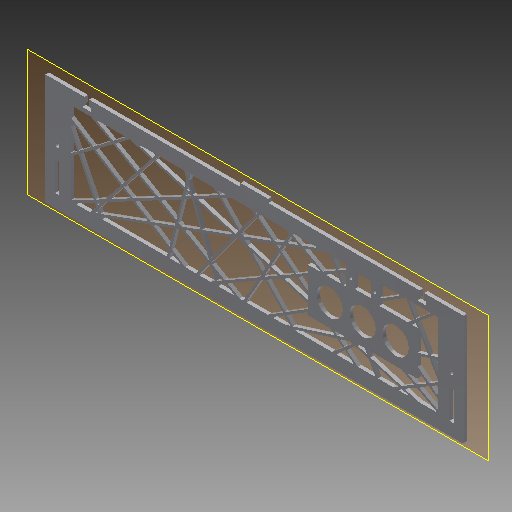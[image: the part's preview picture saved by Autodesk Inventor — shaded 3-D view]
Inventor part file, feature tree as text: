
AUTODESK INVENTOR PART (.ipt)
format: ipt  version: 2019 (Build 230136000, 136)  size: 1,500,160 bytes
history: native  units: in
note: dims shown in document units (in); Inventor stores cm internally (conversion verified against a paired STEP export)
features: fillet x12, extrude x11, sketch x10, other x9, reference x9, hole x3, plane x1
ambient origin geometry x8: Origin, YZ Plane, XZ Plane, XY Plane, X Axis, Y Axis, Z Axis, Center Point
bodies: Solid1 (feature_tree)
feature tree (55):
  plane  "Work Plane1"
  extrude  "BackPanel"  Depth=0.0394in
  fillet  "CornerFillet"  Radius=0.475in
  extrude  "ScrewSlotExtrusion"  Depth=0.3265in
  fillet  "SlotFillets"  Radius=0.1234in
  hole  "Hole1"  [1 undecoded]
  extrude  "BottomTab"  Depth=0.1234in
  fillet  "BottomTabFillet"  Radius=0.125in
  extrude  "Slots"  Depth=1.0in
  fillet  "Fillet4"  Radius=0.0197in
  extrude  "InsideGap"  Depth=1.0in
  fillet  "InsideGapFillet"  Radius=0.125in
  extrude  "Hash1"  Depth=1.054in
  extrude  "Hash2"  Depth=1.054in
  extrude  "BackButtonMount"  Depth=0.125in TaperAngle=0.0deg
  hole  "BackButtonHoles"  [1 undecoded]
  extrude  "USBPortMount"  Depth=0.5in
  extrude  "USBPortHole"  Depth=0.5in
  hole  "USBPortScrewHoles"  [1 undecoded]
  fillet  "GridFillets1"  Radius=0.5in
  fillet  "GridFillets2"  Radius=1.0in
  fillet  "GridFillets3"  Radius=0.0197in
  fillet  "GridFillets4"  Radius=0.0882in
  fillet  "GridFillets5"  Radius=1.15in
  fillet  "GridFillets6"  Radius=2.8in
  fillet  "GridFillets7"  Radius=4.0072in
  extrude  "SmallHoleRemoval"  Depth=0.125in
  sketch  "Sketch1"  dims[d0=0.125in d1=0.0in d2=0.0394in d3=0.475in]
  other  "ScrewSlotSketch"
  reference  "Reference1"
  reference  "Reference2"
  reference  "Reference3"
  other  "ScrewHoleSketch"
  reference  "Reference4"
  reference  "Reference5"
  reference  "Reference6"
  reference  "Reference7"
  other  "BottomTabSketch"
  other  "SlotSketch"
  sketch  "Sketch6"  dims[d5=0.1495in d7=0.3265in d8=0.1234in]
  reference  "Reference18"
  reference  "Reference19"
  sketch  "Sketch7"  dims[d9=0.475in d10=0.1495in]
  sketch  "Sketch8"  dims[d12=0.3265in d13=0.1234in d20=0.125in d21=0.0in]
  sketch  "Sketch9"  dims[d22=1.0in d23=1.0in d24=0.0197in]
  sketch  "Sketch10"  dims[d25=0.1495in]
  sketch  "Sketch12"  dims[d26=0.75in d27=0.375in d28=0.25in d29=0.5635in d30=1.0in d31=0.8108in d32=1.0in d34=0.125in d35=0.0in]
  sketch  "Sketch13"  dims[d36=0.0197in d37=1.054in]
  sketch  "Sketch14"  dims[d39=0.149in d40=1.054in]
  sketch  "Sketch15"  dims[d41=0.149in d42=0.125in d43=0.0in d44=0.0197in d45=0.5in d46=0.5in d47=0.5in d48=0.5in d49=1.0in d50=0.0in d51=0.0197in d52=0.0882in d53=1.15in d54=2.8in d55=4.0072in d56=5.1478in d57=7.3764in d58=8.8266in d59=11.0in d60=2.102in d61=0.4077in d62=0.962in d63=1.017in d64=150.0deg d65=1.0994in d66=0.8225in d67=1.0444in d68=0.7174in d69=0.9826in d70=0.08in d71=0.08in d72=0.08in d73=0.08in d74=0.08in d75=0.08in d76=0.08in d77=0.08in d78=0.08in d79=0.08in d80=6.3348in d81=0.8684in d82=9.9487in d83=0.8831in d84=0.08in d85=0.125in d86=0.0in d87=0.8208in d88=0.4592in d89=1.0588in d90=0.8406in d91=0.702in d92=2.054in d93=150.0deg d94=1.124in d95=4.025in d96=0.7627in d97=5.1in d98=0.916in d99=6.426in d100=0.9702in d101=7.6562in d103=9.2721in d104=0.8139in d105=9.8in d106=0.9786in d107=11.9921in d108=120.0deg d109=0.08in d111=0.08in d112=0.08in d114=0.08in d115=0.08in d116=0.08in d117=0.08in d118=0.08in d119=0.08in d120=0.125in d121=0.0in d122=1.312in d123=0.4978in d124=0.08in d125=0.08in d126=0.08in d127=1.1811in d129=1.1811in d130=2.0in d131=0.7874in d132=0.7874in d133=0.125in d134=0.0in d135=1.1811in d137=1.1811in d138=0.9449in d139=0.75in d140=0.375in d141=0.25in d142=0.5635in d143=1.0in d144=0.8108in d152=1.1811in d156=0.125in d157=0.0in d158=0.5712in d160=0.5318in d161=0.125in d162=0.0in d163=0.8661in d165=0.129in d166=0.75in d167=0.225in d168=0.25in d169=0.5635in d170=1.0in d171=0.8108in d172=0.0197in d173=0.0197in d174=0.0197in d175=0.0197in d176=0.0197in d177=0.0197in d178=0.0197in d179=0.125in d180=0.0in]
  parser-record x1  (decoder bookkeeping rows leaked as tree rows — omitted from the tree; the rows remain in map.json)
  other  "ArcadeController.iam"
  other  "Panel_side:2"
  other  "Panel_side:1"
  other  "BottomPanel:1"
note: 3 required parameter values undecoded (feature->parameter linkage not recoverable at this tier; creation-order binding heuristic only, values carry confidence <= 0.55)
note: 1 file-system path scrubbed to <path> (originals preserved in map.json)
